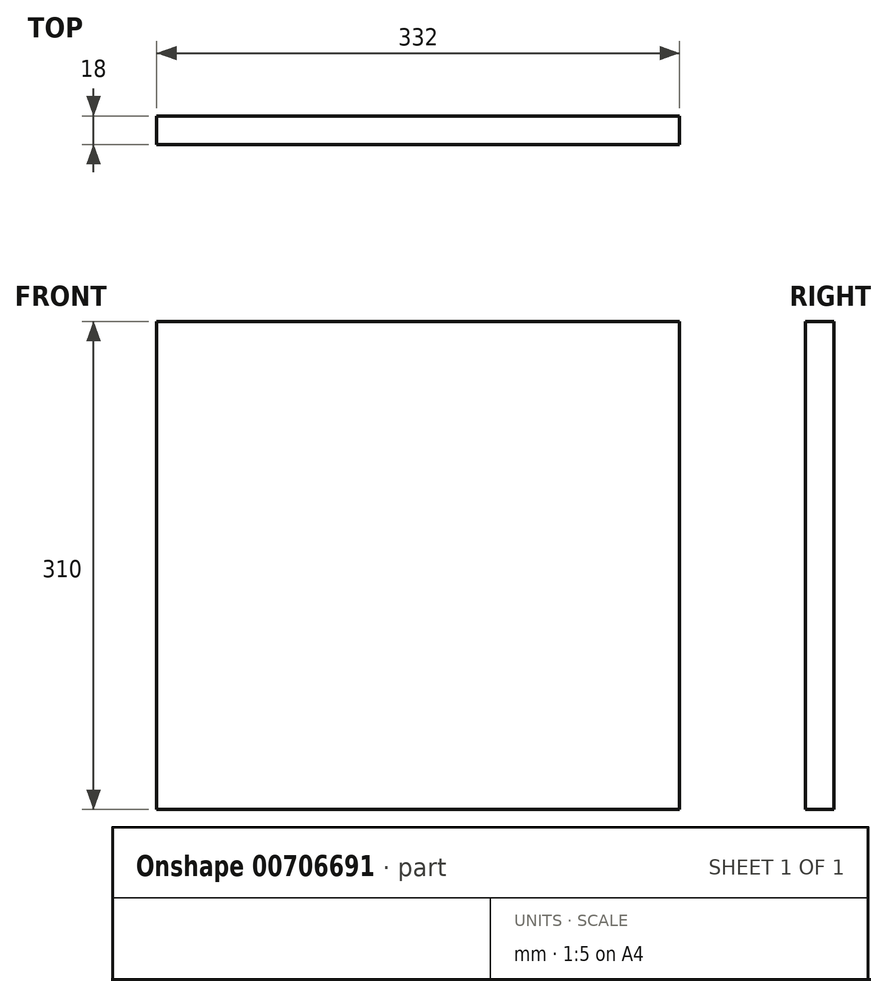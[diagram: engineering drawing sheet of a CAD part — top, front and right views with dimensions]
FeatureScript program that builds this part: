
annotation { "Feature Type Name" : "Feature", "Feature Type Description" : "" }
export const myFeature = defineFeature(function(context is Context, id is Id, definition is map)
    precondition{}
    {
        {
            var Q0;
            Q0=qCreatedBy(makeId("Front.planeOp"),FACE);
            var sketch = newSketch(context, id + "F0", { "sketchPlane" : qUnion([Q0])});
            skLineSegment(sketch, "E0.bottom", {"start": v(-166, -155) * mm, "end": v(166, -155) * mm});
            skLineSegment(sketch, "E0.top", {"start": v(-166, 155) * mm, "end": v(166, 155) * mm});
            skLineSegment(sketch, "E0.left", {"start": v(-166, -155) * mm, "end": v(-166, 155) * mm});
            skLineSegment(sketch, "E0.right", {"start": v(166, -155) * mm, "end": v(166, 155) * mm});
            skPoint(sketch, "E0.middle", {"position": v(0, 0) * mm});
            skSolve(sketch);
        }
        {
            var Q0;
            Q0=makeQuery(id+"F0.imprint","IMPRINT",FACE,{"disambiguationData":[TD([[makeQuery(id+"F0.imprint","IMPRINT",EDGE,{"derivedFrom":sQuery(id+"F0.wireOp",EDGE,"E0.bottom")}),1.0]])]});
            extrude(context, id + "F1", {"entities" : qUnion([Q0]), "depth" : 18 * mm, "offsetDistance" : 25 * mm, "symmetric" : true});
        }
    });
